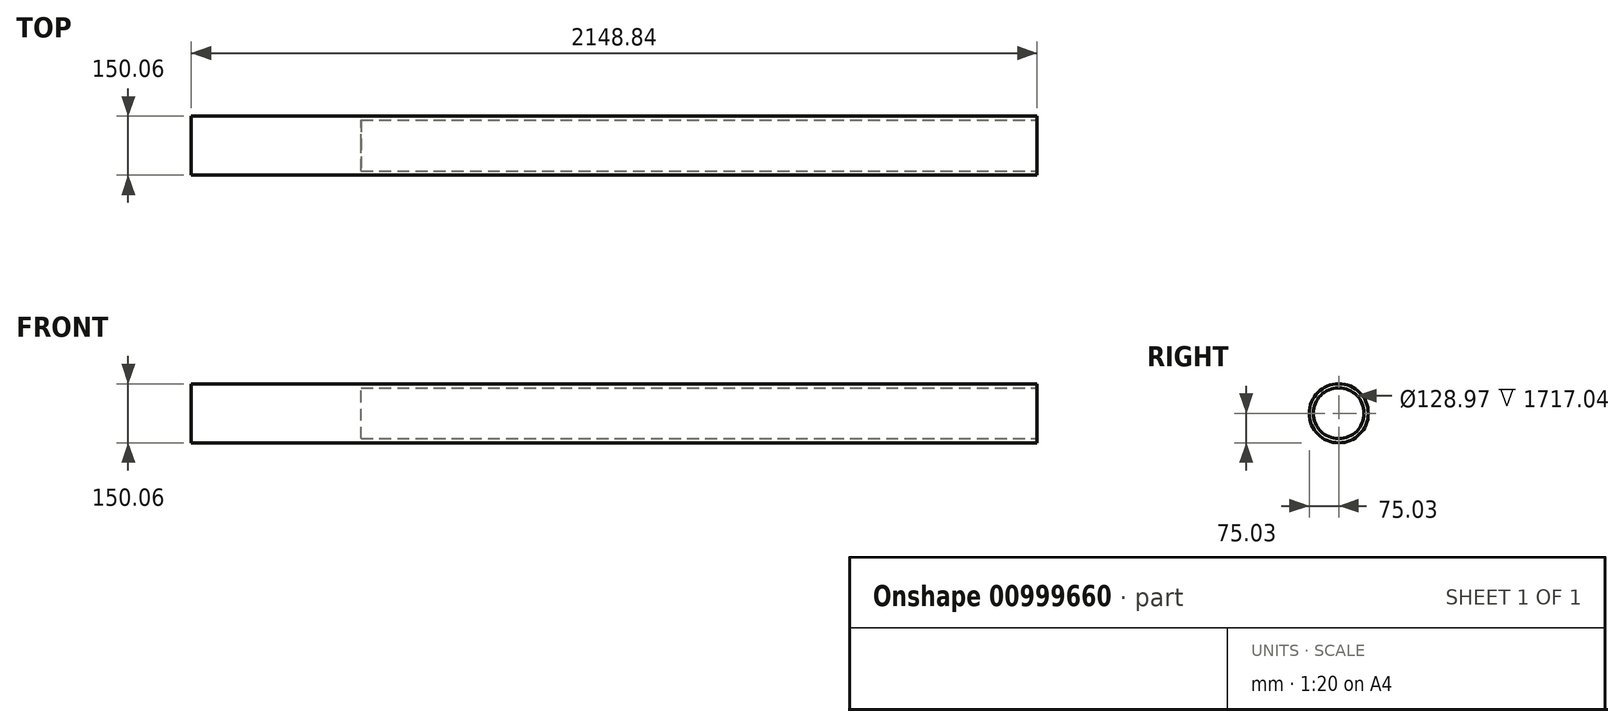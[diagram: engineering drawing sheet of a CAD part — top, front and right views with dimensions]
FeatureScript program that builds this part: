
annotation { "Feature Type Name" : "Feature", "Feature Type Description" : "" }
export const myFeature = defineFeature(function(context is Context, id is Id, definition is map)
    precondition{}
    {
        {
            var Q0;
            Q0=qCreatedBy(makeId("Right.planeOp"),FACE);
            var sketch = newSketch(context, id + "F0", { "sketchPlane" : qUnion([Q0])});
            skCircle(sketch, "E0", {"center": v(0, 0) * mm, "radius": 75.03 * mm});
            skSolve(sketch);
        }
        {
            var Q0;
            Q0 = qSketchRegion(id + "F0", true);
            extrude(context, id + "F1", {"entities" : qUnion([Q0]), "depth" : 2148.84 * mm, "offsetDistance" : 25.4 * mm});
        }
        {
            var Q0;
            Q0=makeQuery(id+"F1.opExtrude","CAP_FACE",FACE,{"disambiguationData":[OSD([sQuery(id+"F0.wireOp",EDGE,"E0")])],"isStart":false});
            var sketch = newSketch(context, id + "F2", { "sketchPlane" : qUnion([Q0])});
            skCircle(sketch, "E1", {"center": v(0, 0) * mm, "radius": 64.49 * mm});
            skSolve(sketch);
        }
        {
            var Q0;
            Q0 = qSketchRegion(id + "F2", true);
            extrude(context, id + "F3", {"entities" : qUnion([Q0]), "operationType" : NewBodyOperationType.REMOVE, "oppositeDirection" : true, "depth" : 203.2 * mm, "offsetDistance" : 25.4 * mm});
        }
        {
            var Q0;
            Q0=makeQuery(id+"F3.boolean.opBoolean","COPY",FACE,{"derivedFrom":makeQuery(id+"F3.opExtrude","CAP_FACE",FACE,{"disambiguationData":[OSD([sQuery(id+"F2.wireOp",EDGE,"E1")])],"isStart":false})});
            extrude(context, id + "F4", {"entities" : qUnion([Q0]), "operationType" : NewBodyOperationType.REMOVE, "oppositeDirection" : true, "depth" : 1513.84 * mm, "offsetDistance" : 25.4 * mm});
        }
    });
